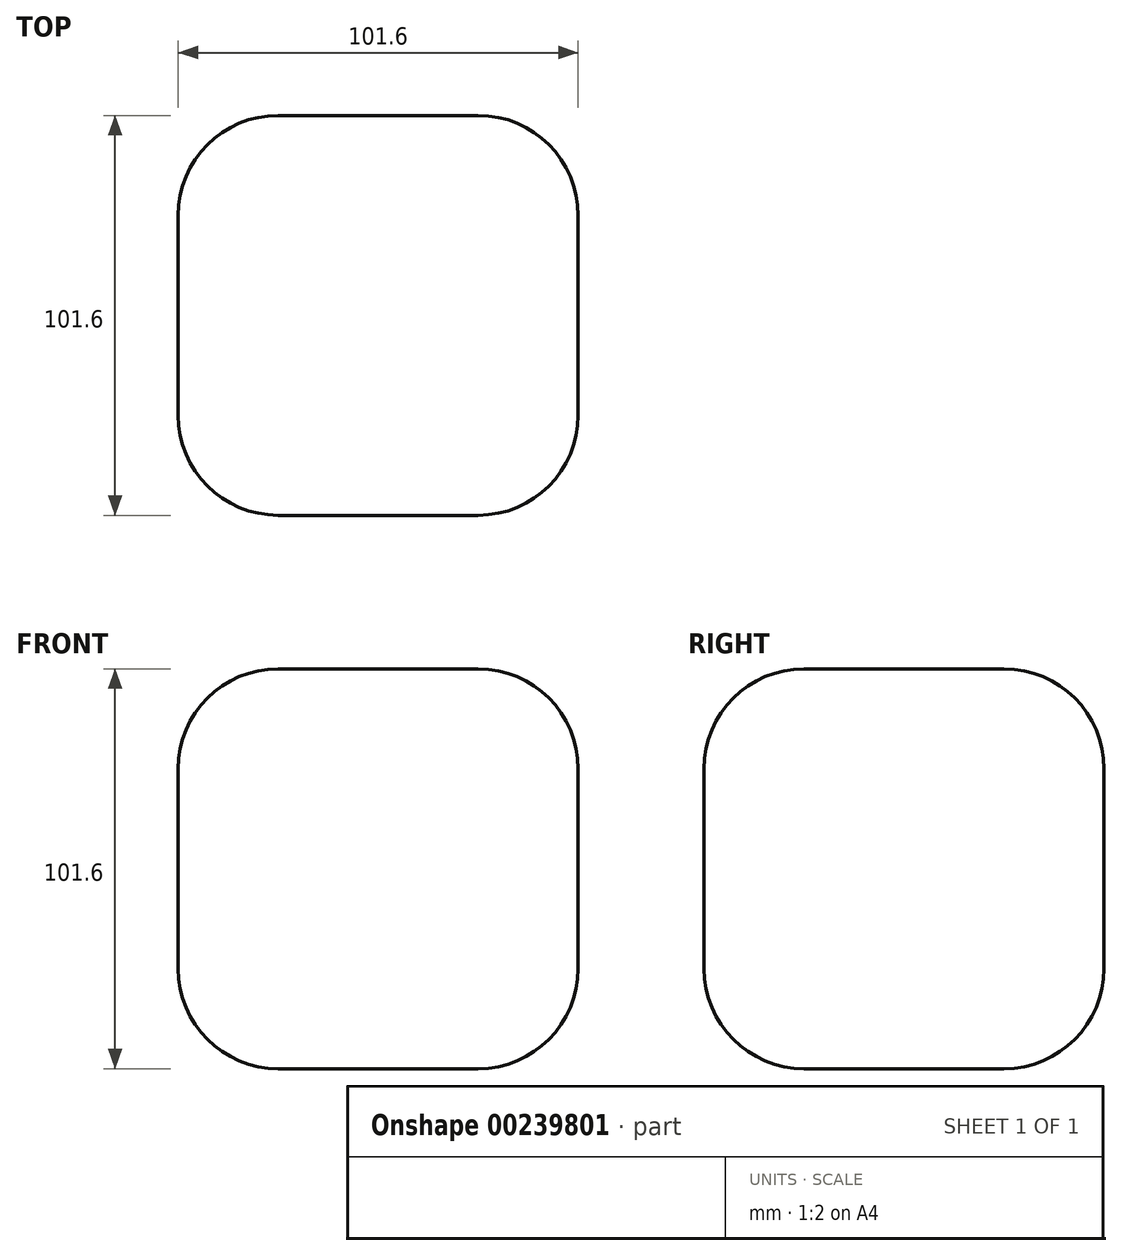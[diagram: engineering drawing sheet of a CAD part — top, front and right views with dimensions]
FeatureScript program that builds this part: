
annotation { "Feature Type Name" : "Feature", "Feature Type Description" : "" }
export const myFeature = defineFeature(function(context is Context, id is Id, definition is map)
    precondition{}
    {
        {
            var Q0;
            Q0=qCreatedBy(makeId("Top.planeOp"),FACE);
            var sketch = newSketch(context, id + "F0", { "sketchPlane" : qUnion([Q0])});
            skLineSegment(sketch, "E0.bottom", {"start": v(0, 0) * mm, "end": v(101.6, 0) * mm});
            skLineSegment(sketch, "E0.top", {"start": v(0, 101.6) * mm, "end": v(101.6, 101.6) * mm});
            skLineSegment(sketch, "E0.left", {"start": v(0, 0) * mm, "end": v(0, 101.6) * mm});
            skLineSegment(sketch, "E0.right", {"start": v(101.6, 0) * mm, "end": v(101.6, 101.6) * mm});
            skSolve(sketch);
        }
        {
            var Q0;
            Q0=makeQuery(id+"F0.imprint","IMPRINT",FACE,{"disambiguationData":[TD([[makeQuery(id+"F0.imprint","IMPRINT",EDGE,{"derivedFrom":sQuery(id+"F0.wireOp",EDGE,"E0.bottom")}),1.0]])]});
            extrude(context, id + "F1", {"entities" : qUnion([Q0]), "depth" : 101.6 * mm});
        }
        {
            var Q0;
            Q0=makeQuery(id+"F1.opExtrude","CAP_EDGE",EDGE,{"disambiguationData":[OSD([sQuery(id+"F0.wireOp",EDGE,"E0.bottom")])],"isStart":false});
            var Q1;
            Q1=makeQuery(id+"F1.opExtrude","CAP_EDGE",EDGE,{"disambiguationData":[OSD([sQuery(id+"F0.wireOp",EDGE,"E0.right")])],"isStart":false});
            var Q2;
            Q2=makeQuery(id+"F1.opExtrude","CAP_EDGE",EDGE,{"disambiguationData":[OSD([sQuery(id+"F0.wireOp",EDGE,"E0.left")])],"isStart":false});
            var Q3;
            Q3=makeQuery(id+"F1.opExtrude","CAP_EDGE",EDGE,{"disambiguationData":[OSD([sQuery(id+"F0.wireOp",EDGE,"E0.top")])],"isStart":false});
            var Q4;
            Q4=makeQuery(id+"F1.opExtrude","SWEPT_FACE",FACE,{"disambiguationData":[OSD([sQuery(id+"F0.wireOp",EDGE,"E0.bottom")])]});
            var Q5;
            Q5=makeQuery(id+"F1.opExtrude","CAP_EDGE",EDGE,{"disambiguationData":[OSD([sQuery(id+"F0.wireOp",EDGE,"E0.right")])],"isStart":true});
            var Q6;
            Q6=makeQuery(id+"F1.opExtrude","SWEPT_EDGE",EDGE,{"disambiguationData":[OSD([sQuery(id+"F0.wireOp",EDGE,"E0.top"),sQuery(id+"F0.wireOp",EDGE,"E0.right")])]});
            var Q7;
            Q7=makeQuery(id+"F1.opExtrude","CAP_EDGE",EDGE,{"disambiguationData":[OSD([sQuery(id+"F0.wireOp",EDGE,"E0.top")])],"isStart":true});
            var Q8;
            Q8=makeQuery(id+"F1.opExtrude","SWEPT_EDGE",EDGE,{"disambiguationData":[OSD([sQuery(id+"F0.wireOp",EDGE,"E0.top"),sQuery(id+"F0.wireOp",EDGE,"E0.left")])]});
            var Q9;
            Q9=makeQuery(id+"F1.opExtrude","CAP_EDGE",EDGE,{"disambiguationData":[OSD([sQuery(id+"F0.wireOp",EDGE,"E0.left")])],"isStart":true});
            fillet(context, id + "F2", {"entities" : qUnion([Q0, Q1, Q2, Q3, Q4, Q5, Q6, Q7, Q8, Q9]), "radius" : 25.4 * mm, "tangentPropagation" : true, "allowEdgeOverflow" : false});
        }
    });
